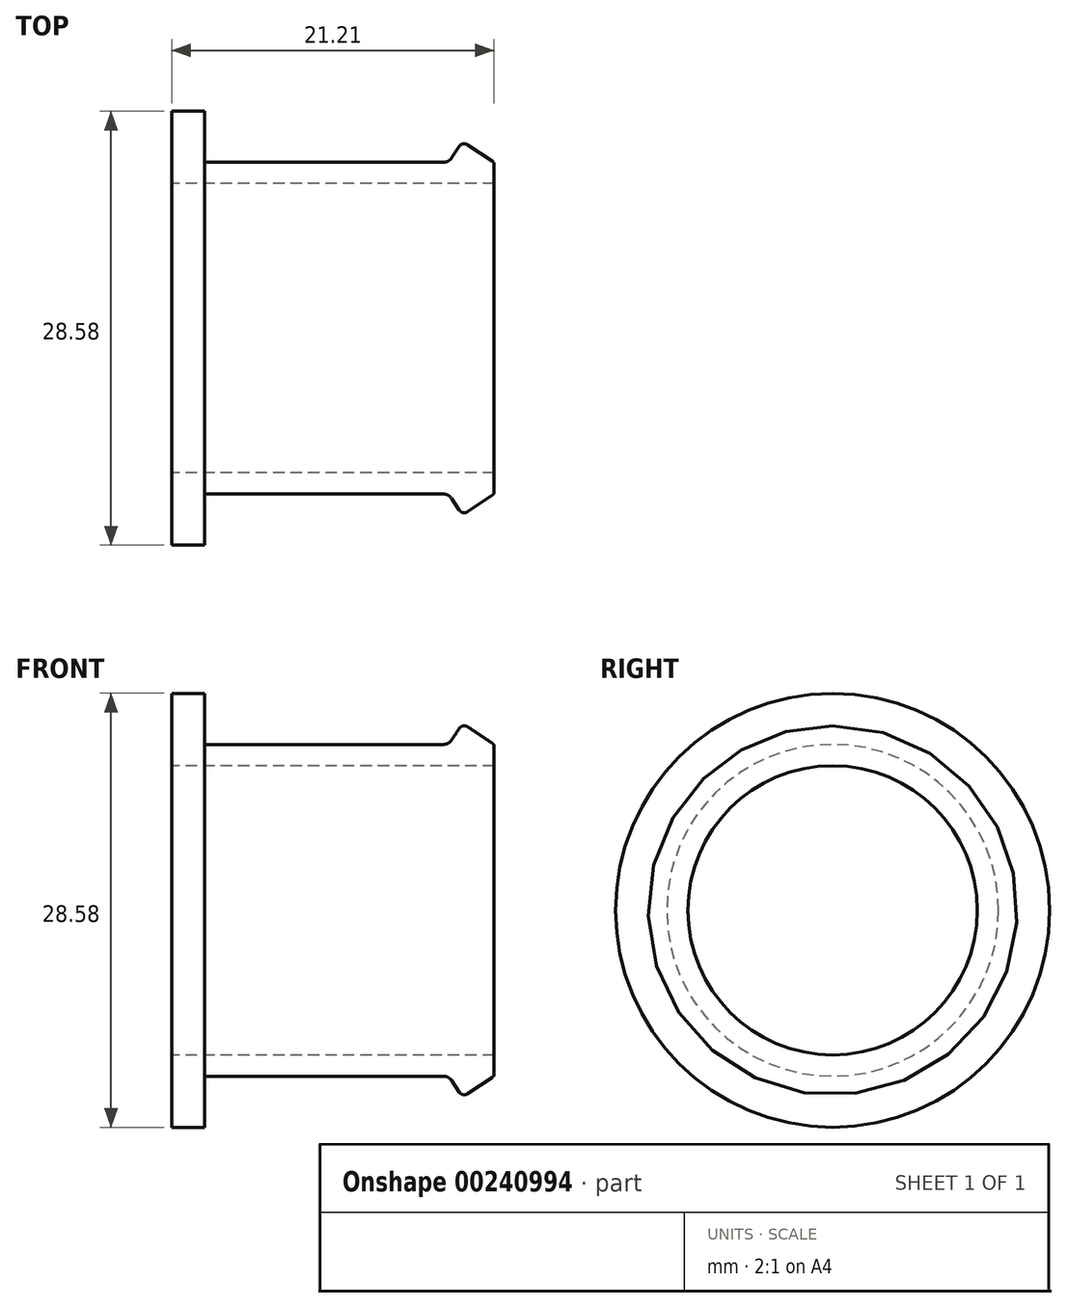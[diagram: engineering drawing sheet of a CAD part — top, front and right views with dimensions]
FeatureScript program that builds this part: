
annotation { "Feature Type Name" : "Feature", "Feature Type Description" : "" }
export const myFeature = defineFeature(function(context is Context, id is Id, definition is map)
    precondition{}
    {
        {
            var Q0;
            Q0=qCreatedBy(makeId("Top.planeOp"),FACE);
            var sketch = newSketch(context, id + "F0", { "sketchPlane" : qUnion([Q0])});
            skLineSegment(sketch, "E0.top", {"start": v(-1.08, 14.29) * mm, "end": v(1.08, 14.29) * mm});
            skPoint(sketch, "E0.middle", {"position": v(0, 0) * mm});
            skLineSegment(sketch, "E1.top", {"start": v(1.08, 9.53) * mm, "end": v(20.13, 9.53) * mm});
            skPoint(sketch, "E1.centerSnap0", {"position": v(1.08, 0) * mm});
            skLineSegment(sketch, "E2.bottom", {"start": v(16.8, 10.92) * mm, "end": v(1.08, 10.92) * mm});
            skLineSegment(sketch, "E2.left", {"start": v(20.13, 10.8) * mm, "end": v(20.13, 9.53) * mm});
            skPoint(sketch, "E2.middle", {"position": v(10.6, 0) * mm});
            skLineSegment(sketch, "E3", {"start": v(1.08, 9.53) * mm, "end": v(-1.08, 9.53) * mm});
            skLineSegment(sketch, "E4.trimOffspring", {"start": v(-1.08, 9.53) * mm, "end": v(-1.08, 14.29) * mm});
            skLineSegment(sketch, "E5.trimOffspring", {"start": v(1.08, 10.92) * mm, "end": v(1.08, 14.29) * mm});
            skLineSegment(sketch, "E6", {"start": v(20.03, 11) * mm, "end": v(18.38, 12.09) * mm});
            skLineSegment(sketch, "E7", {"start": v(17.85, 11.98) * mm, "end": v(17.33, 11.2) * mm});
            skPoint(sketch, "E8.visualSharp", {"position": v(20.13, 10.92) * mm});
            skArc(sketch, "E8.filletArc", {"start": v(20.13, 10.8) * mm, "mid": v(20.1, 10.9) * mm, "end": v(20.03, 11) * mm});
            skPoint(sketch, "E9.visualSharp", {"position": v(18.06, 12.3) * mm});
            skArc(sketch, "E9.filletArc", {"start": v(18.38, 12.09) * mm, "mid": v(18.1, 12.15) * mm, "end": v(17.85, 11.98) * mm});
            skPoint(sketch, "E10.visualSharp", {"position": v(17.14, 10.92) * mm});
            skArc(sketch, "E10.filletArc", {"start": v(16.8, 10.92) * mm, "mid": v(17.1, 11) * mm, "end": v(17.33, 11.2) * mm});
            skLineSegment(sketch, "E11", {"start": v(-5.08, 0) * mm, "end": v(23.79, 0) * mm, "construction": true});
            skSolve(sketch);
        }
        {
            var Q0;
            Q0=makeQuery(id+"F0.imprint","IMPRINT",FACE,{"disambiguationData":[TD([[makeQuery(id+"F0.imprint","IMPRINT",EDGE,{"derivedFrom":sQuery(id+"F0.wireOp",EDGE,"E0.top")}),-1.0]])]});
            var Q1;
            Q1=sQuery(id+"F0.wireOp",EDGE,"E11");
            revolve(context, id + "F1", {"entities" : qUnion([Q0]), "axis" : qUnion([Q1]), "revolveType" : RevolveType.FULL});
        }
    });
